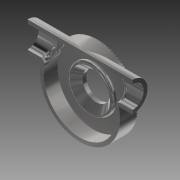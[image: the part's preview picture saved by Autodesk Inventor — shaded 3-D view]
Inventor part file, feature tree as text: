
AUTODESK INVENTOR PART (.ipt)
format: ipt  version: 2013 (Build 170138000, 138)  size: 707,072 bytes
history: native  units: mm
features: sketch x5, other x3, fillet x3, revolve x2, extrude x2, plane x1, pattern_circular x1
ambient origin geometry x8: Origin, YZ Plane, XZ Plane, XY Plane, X Axis, Y Axis, Z Axis, Center Point
feature tree (17):
  other  "Sólido1"
  sketch  "Boceto1"  dims[d0=0.5mm d8=7.0mm d9=6.0mm]
  revolve  "Revolución1"  [1 undecoded]
  fillet  "Empalme1"  Radius=6.0mm
  plane  "Plano de trabajo1"
  sketch  "Boceto2"  dims[d10=1.5mm d11=4.5mm]
  extrude  "Extrusión2"  Depth=4.5mm
  other  "Suprimir cara1"
  revolve  "Revolución2"  Angle=90.0deg
  fillet  "Empalme5"  Radius=2.0mm
  extrude  "Extrusión3"  Depth=1.0mm
  pattern_circular  "Patrón circular2"  [2 undecoded]
  fillet  "Empalme7"  Radius=6.0mm
  other  "Suprimir cara3"
  sketch  "Boceto5"  dims[d18=-8.0mm d20=1.0mm]
  sketch  "Boceto6"  dims[d21=0.5mm d23=0.5mm d30=6.0mm d37=1.5mm d38=9.0mm d39=42.0mm d40=0.0mm d42=90.0deg d44=2.0mm d46=42.0mm d47=0.0mm d48=940.0mm d49=360.0deg d60=1.0mm d61=1.5mm]
  sketch  "Boceto3"  dims[d13=1.5mm d15=90.0deg d16=2.0mm]
note: 3 required parameter values undecoded (feature->parameter linkage not recoverable at this tier; creation-order binding heuristic only, values carry confidence <= 0.55)